# Revit family: Dämmelement 45
name_source: partatom
category: HLS-Bauteile
revit_build: Autodesk Revit 2017 (Build: 20190507_1515(x64)
units: mm (PartAtom-declared; Revit-internal decimal feet)

## family parameters
Arbeitsebenenbasiert = Ja
Beim Laden mit Abzugskörper schneiden = Nein
Bemaßung runder Anschluss = Durchmesser verwenden
Gemeinsam genutzt = Ja
Immer vertikal = Nein
Raumberechnungspunkt = Nein
Teiletyp = Normal

## types (1)
- Dämmelement 45
    Anschluss = M8x50
    Artikelnummer = 0783396
    EAN = 4250928418791
    Fabrikat = MEFA
    Firma = MEFA Befestigungs- und Montagesysteme GmbH
    Gewicht = 0.17 kg
    Gewicht pro Bauteil = 0.17 kg
    Höhe = 50 mm
    Kurztext1 = Dämmelement für C-Profil 45
    Kurztext2 = Anschluss M8x50 Hammerkopf 40x22
    Lasttyp = 40x22
    Material = Stahl
    Material Dämmelement = Gummi SBR
    Mengeneinheit = St
    Oberflaeche = galvanisch verzinkt
    Shore-Härte = 60 ± 5 Shore
    Vorgabe-Ansicht = 1219 mm
    max. Temperaturbeständigkeit = 100 °C
    max. zul. Last Druck = 1.30 kN
    passend für = C-Profil 45/26, 45/45, 45/60, 45/75
    vpe = 1 St

## geometry (parser evidence)
native form markers: Sweep x1
no freeform markers — native parametric forms only
